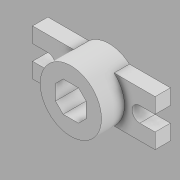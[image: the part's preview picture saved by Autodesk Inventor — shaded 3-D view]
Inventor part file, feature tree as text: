
AUTODESK INVENTOR PART (.ipt)
format: ipt  version: 2020 (Build 240168000, 168)  size: 134,144 bytes
history: native  units: mm
features: extrude x3, sketch x3, other x1
ambient origin geometry x8: Origin, YZ Plane, XZ Plane, XY Plane, X Axis, Y Axis, Z Axis, Center Point
bodies: Body1 (feature_tree)
feature tree (7):
  other  "Sólido1"
  extrude  "Extrusión1"  Depth=60.0mm
  extrude  "Extrusión2"  Depth=20.0mm
  extrude  "Extrusión3"  Depth=20.0mm
  sketch  "Boceto1"  dims[d2=160.0mm d3=60.0mm]
  sketch  "Boceto2"  dims[d4=20.0mm d5=20.0mm]
  sketch  "Boceto3"  dims[d6=20.0mm d7=20.0mm d8=20.0mm d9=0.0mm d10=80.0mm d11=30.0mm d12=20.0mm d13=0.0mm d14=0.0mm d15=40.0mm d16=40.0mm d17=10.0mm d18=10.0mm d19=10.0mm d20=10.0mm d21=10.0mm d22=10.0mm d23=10.0mm d24=10.0mm d25=0.0mm d26=0.0mm]
